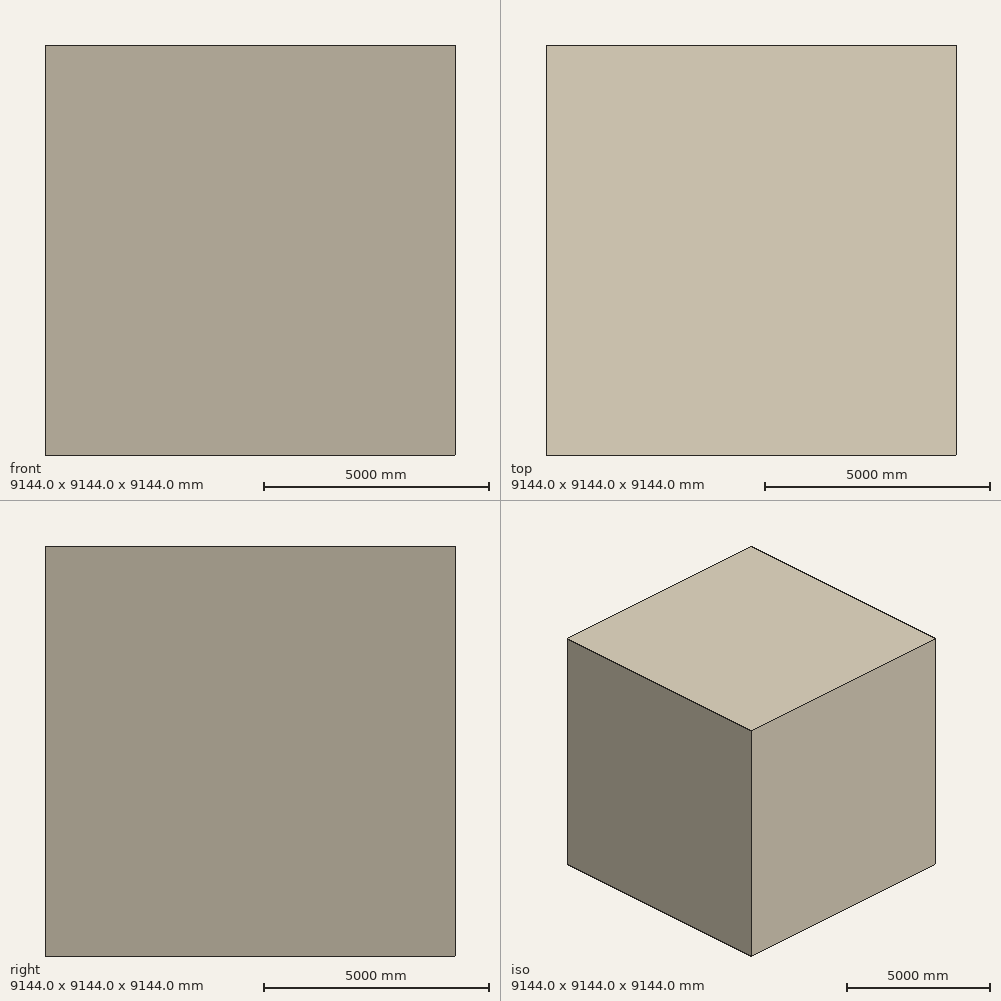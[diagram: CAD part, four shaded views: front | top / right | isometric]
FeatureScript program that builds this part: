
annotation { "Feature Type Name" : "Feature", "Feature Type Description" : "" }
export const myFeature = defineFeature(function(context is Context, id is Id, definition is map)
    precondition{}
    {
        {
            var Q0;
            Q0=qCreatedBy(makeId("Top.planeOp"),FACE);
            var sketch = newSketch(context, id + "F0", { "sketchPlane" : qUnion([Q0])});
            skLineSegment(sketch, "E0.bottom", {"start": v(-4572, -4572) * mm, "end": v(4572, -4572) * mm});
            skLineSegment(sketch, "E0.top", {"start": v(-4572, 4572) * mm, "end": v(4572, 4572) * mm});
            skLineSegment(sketch, "E0.left", {"start": v(-4572, -4572) * mm, "end": v(-4572, 4572) * mm});
            skLineSegment(sketch, "E0.right", {"start": v(4572, -4572) * mm, "end": v(4572, 4572) * mm});
            skPoint(sketch, "E0.middle", {"position": v(0, 0) * mm});
            skSolve(sketch);
        }
        {
            var Q0;
            Q0 = qSketchRegion(id + "F0", true);
            extrude(context, id + "F1", {"entities" : qUnion([Q0]), "depth" : 9144 * mm, "offsetDistance" : 25.4 * mm});
        }
    });
